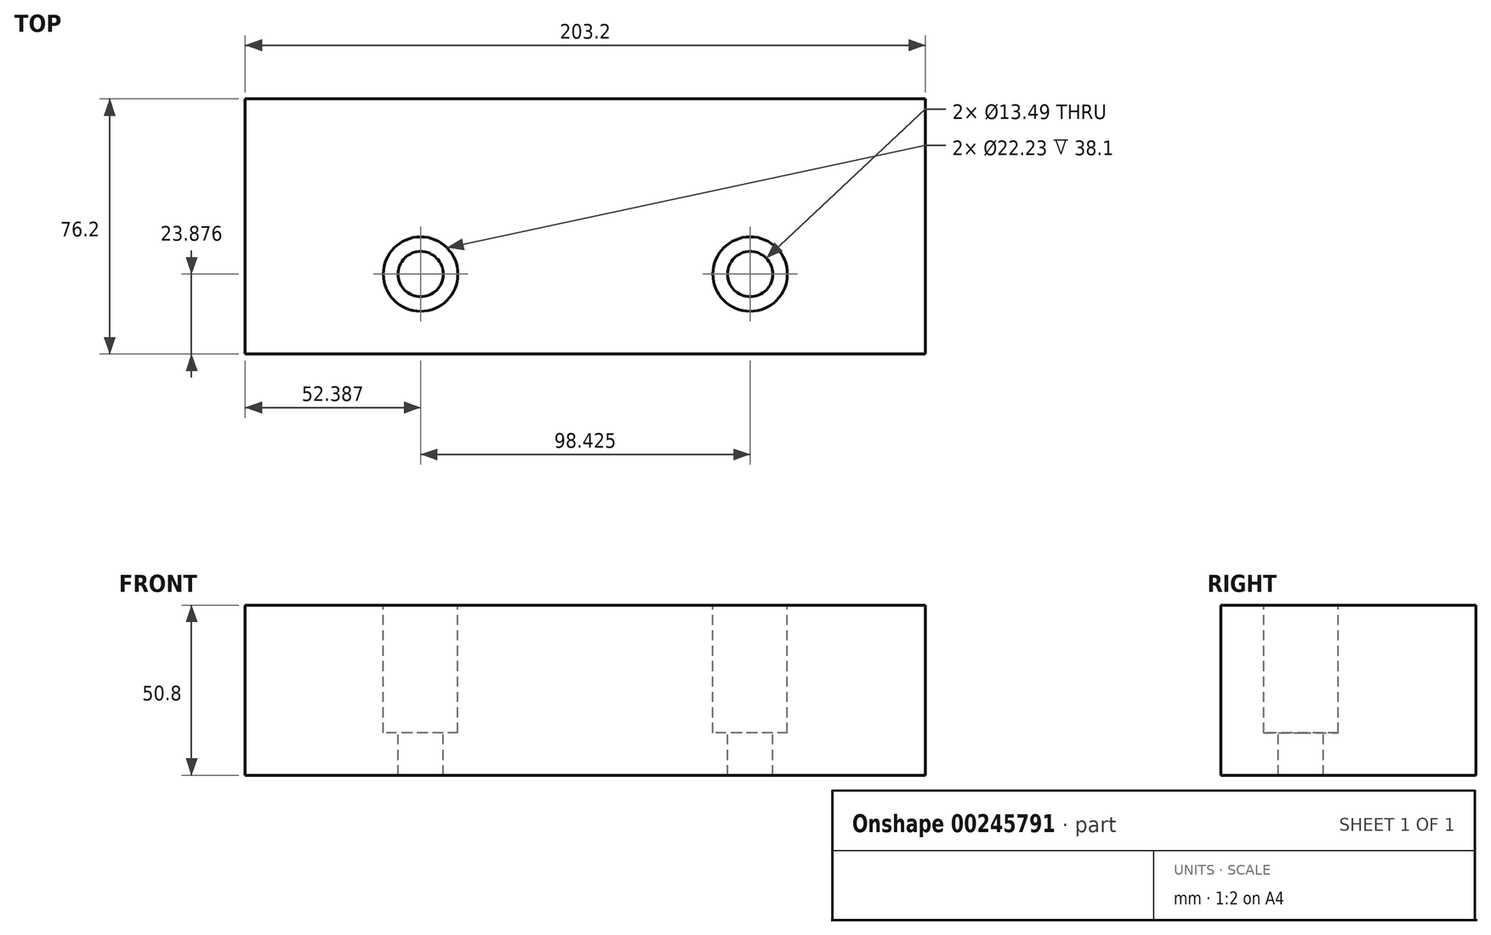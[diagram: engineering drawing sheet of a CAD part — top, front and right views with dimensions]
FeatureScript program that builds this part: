
annotation { "Feature Type Name" : "Feature", "Feature Type Description" : "" }
export const myFeature = defineFeature(function(context is Context, id is Id, definition is map)
    precondition{}
    {
        {
            var Q0;
            Q0=qCreatedBy(makeId("Top.planeOp"),FACE);
            var sketch = newSketch(context, id + "F0", { "sketchPlane" : qUnion([Q0])});
            skLineSegment(sketch, "E0.bottom", {"start": v(101.6, 38.1) * mm, "end": v(-101.6, 38.1) * mm});
            skLineSegment(sketch, "E0.top", {"start": v(101.6, -38.1) * mm, "end": v(-101.6, -38.1) * mm});
            skLineSegment(sketch, "E0.left", {"start": v(101.6, 38.1) * mm, "end": v(101.6, -38.1) * mm});
            skLineSegment(sketch, "E0.right", {"start": v(-101.6, 38.1) * mm, "end": v(-101.6, -38.1) * mm});
            skPoint(sketch, "E0.middle", {"position": v(0, 0) * mm});
            skLineSegment(sketch, "E1", {"start": v(0, 38.1) * mm, "end": v(0, -38.1) * mm, "construction": true});
            skSolve(sketch);
        }
        {
            var Q0;
            Q0=makeQuery(id+"F0.imprint","IMPRINT",FACE,{"disambiguationData":[TD([[makeQuery(id+"F0.imprint","IMPRINT",EDGE,{"derivedFrom":sQuery(id+"F0.wireOp",EDGE,"E0.bottom")}),1.0]])]});
            extrude(context, id + "F1", {"entities" : qUnion([Q0]), "depth" : 50.8 * mm});
        }
        {
            var Q0;
            Q0=makeQuery(id+"F1.opExtrude","CAP_FACE",FACE,{"disambiguationData":[OSD([sQuery(id+"F0.wireOp",EDGE,"E0.bottom"),sQuery(id+"F0.wireOp",EDGE,"E0.top"),sQuery(id+"F0.wireOp",EDGE,"E0.left"),sQuery(id+"F0.wireOp",EDGE,"E0.right")])],"isStart":false});
            var sketch = newSketch(context, id + "F2", { "sketchPlane" : qUnion([Q0])});
            skPoint(sketch, "E2", {"position": v(-49.21, -14.22) * mm});
            skLineSegment(sketch, "E3", {"start": v(0, 38.1) * mm, "end": v(0, -38.1) * mm, "construction": true});
            skPoint(sketch, "E4.MirrorP", {"position": v(49.21, -14.22) * mm});
            skSolve(sketch);
        }
        {
            var Q0;
            Q0=sQuery(id+"F2.wireOp",VERTEX,"E2");
            var Q1;
            Q1=sQuery(id+"F2.wireOp",VERTEX,"E4.MirrorP");
            var Q2;
            Q2=makeQuery(id+"F1.opExtrude","SWEPT_BODY",BODY,{"disambiguationData":[OSD([sQuery(id+"F0.wireOp",EDGE,"E0.bottom"),sQuery(id+"F0.wireOp",EDGE,"E0.top"),sQuery(id+"F0.wireOp",EDGE,"E0.left"),sQuery(id+"F0.wireOp",EDGE,"E0.right")])]});
            hole(context, id + "F3", {"style" : HoleStyle.C_BORE, "endStyle" : HoleEndStyle.THROUGH, "holeDiameter" : 13.5 * mm, "cBoreDiameter" : 22.22 * mm, "cBoreDepth" : 38.1 * mm, "tappedDepth" : 12.7 * mm, "tapClearance" : 3, "startFromSketch" : true, "locations" : qUnion([Q0, Q1]), "scope" : qUnion([Q2])});
        }
    });
